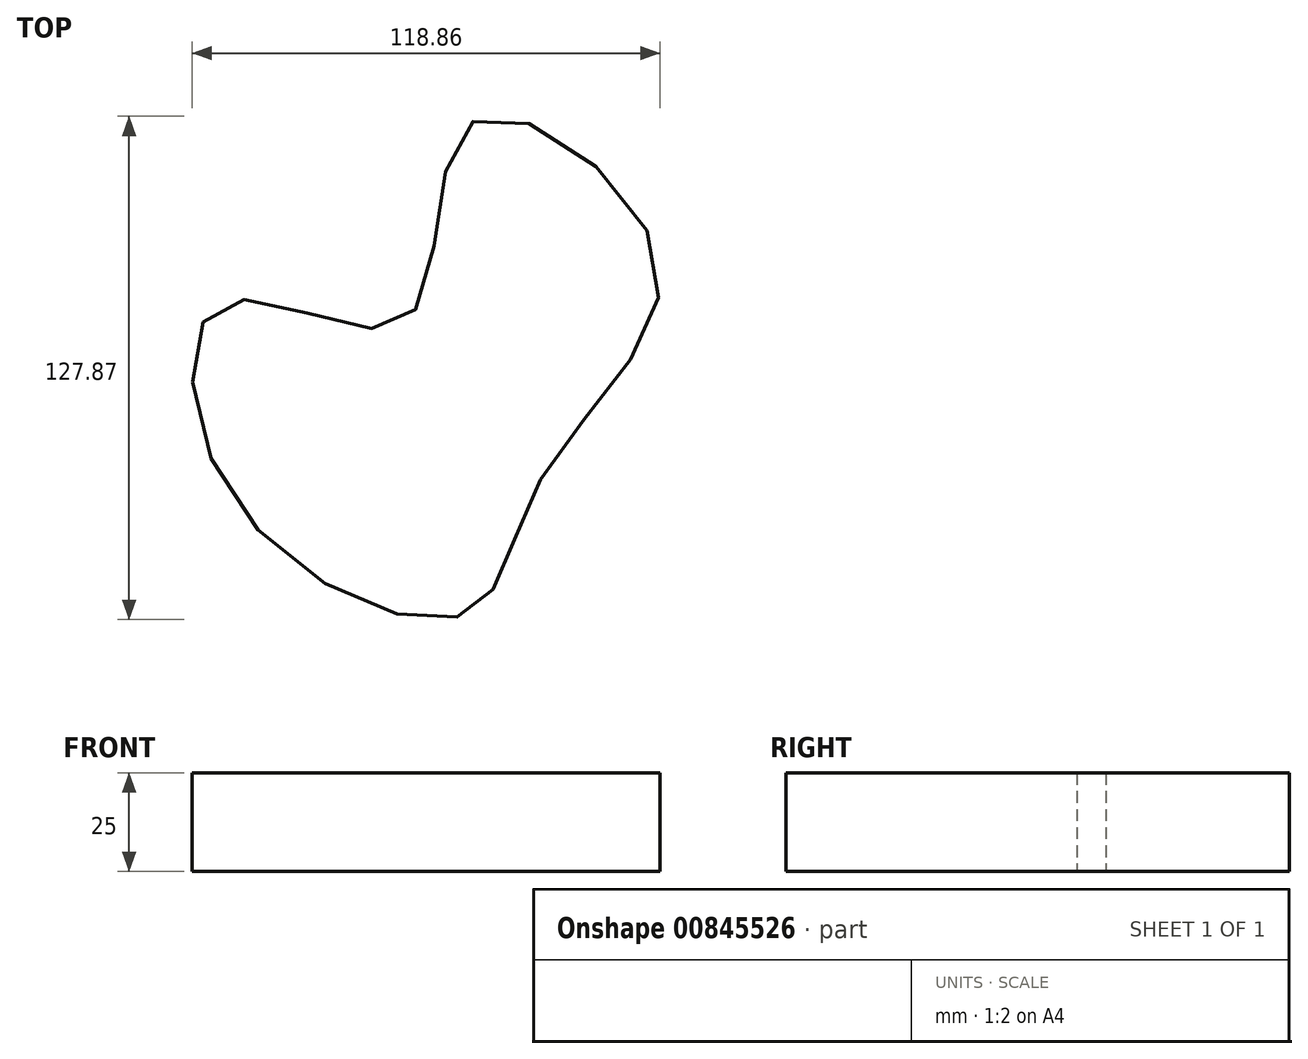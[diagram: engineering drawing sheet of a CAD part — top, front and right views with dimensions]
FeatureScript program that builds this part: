
annotation { "Feature Type Name" : "Feature", "Feature Type Description" : "" }
export const myFeature = defineFeature(function(context is Context, id is Id, definition is map)
    precondition{}
    {
        {
            var Q0;
            Q0=qCreatedBy(makeId("Top.planeOp"),FACE);
            var sketch = newSketch(context, id + "F0", { "sketchPlane" : qUnion([Q0])});
            skFitSpline(sketch, "E0", {"points": [v(-49.7, -27.72) * mm, v(-19.94, 28.25) * mm, v(-67.18, 63.04) * mm, v(-84.1, 12.54) * mm, v(-129.53, 17.34) * mm, v(-128.06, -32.24) * mm, v(-68.71, -61.97) * mm, v(-49.7, -27.72) * mm]});
            skSolve(sketch);
        }
        {
            var Q0;
            Q0 = qSketchRegion(id + "F0", true);
            extrude(context, id + "F1", {"entities" : qUnion([Q0]), "depth" : 25 * mm, "offsetDistance" : 25 * mm});
        }
    });
